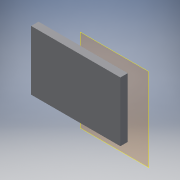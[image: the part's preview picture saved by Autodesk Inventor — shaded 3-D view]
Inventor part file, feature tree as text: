
AUTODESK INVENTOR PART (.ipt)
format: ipt  version: 2016 (Build 200138000, 138)  size: 88,576 bytes
history: native  units: in
note: dims shown in document units (in); Inventor stores cm internally (conversion verified against a paired STEP export)
features: plane x1, extrude x1, sketch x1, reference x1
ambient origin geometry x8: Origin, YZ Plane, XZ Plane, XY Plane, X Axis, Y Axis, Z Axis, Center Point
bodies: Solid1 (feature_tree)
feature tree (4):
  plane  "Work Plane1"
  extrude  "Extrusion1"  Depth=6.2992in
  sketch  "Sketch1"  dims[d0=9.4488in d1=6.2992in d2=0.7874in d3=0.0in]
  reference  "Reference1"
